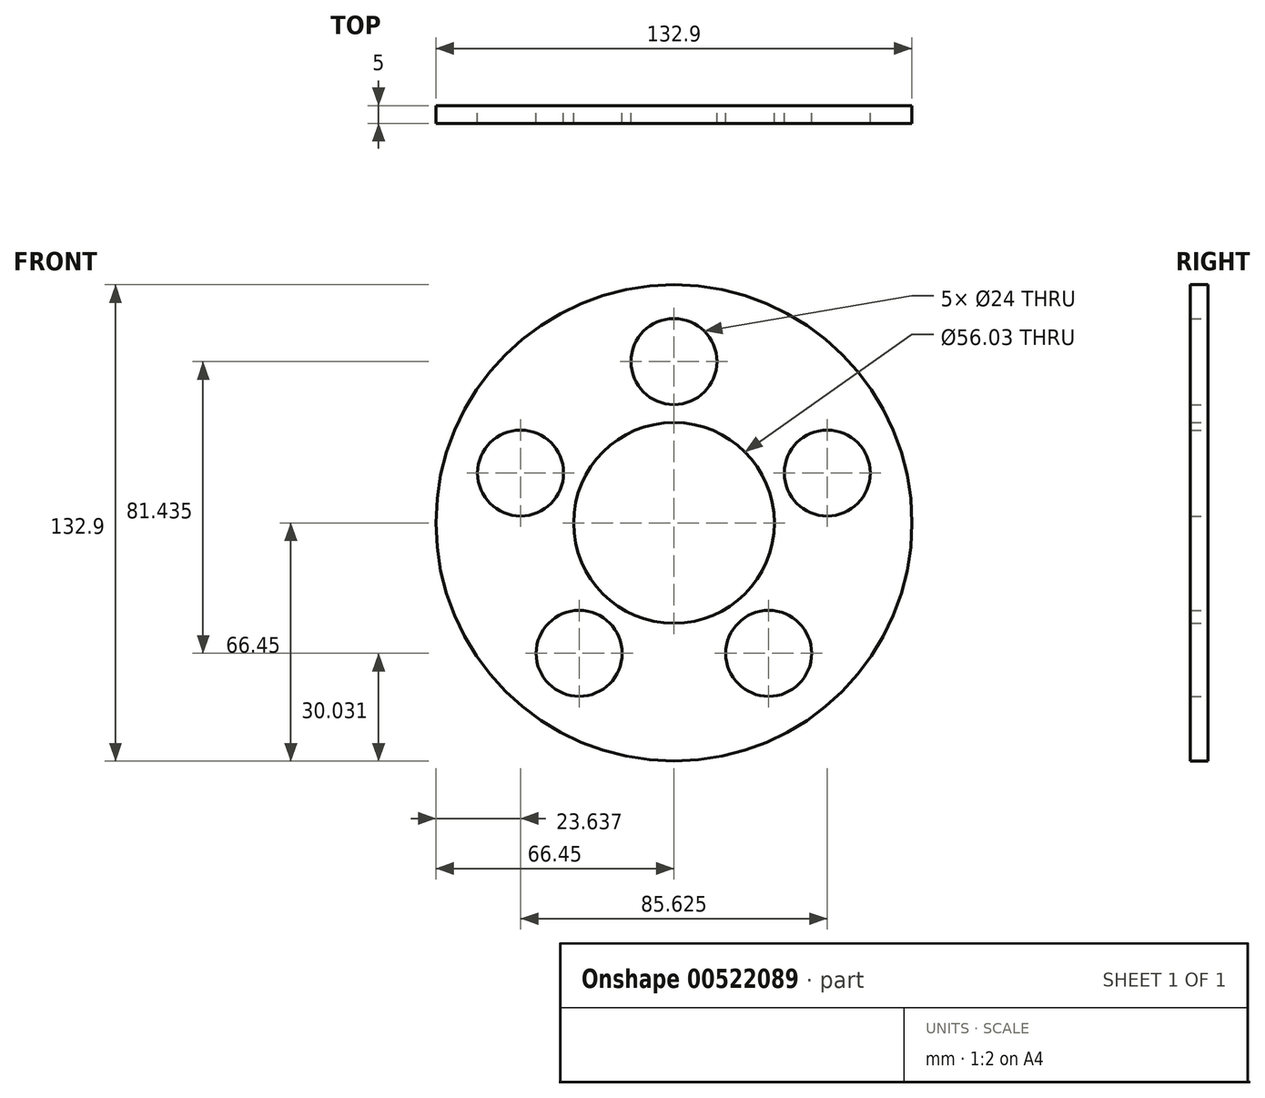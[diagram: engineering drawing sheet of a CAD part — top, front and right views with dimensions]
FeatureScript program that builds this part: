
annotation { "Feature Type Name" : "Feature", "Feature Type Description" : "" }
export const myFeature = defineFeature(function(context is Context, id is Id, definition is map)
    precondition{}
    {
        {
            var Q0;
            Q0=qCreatedBy(makeId("Front.planeOp"),FACE);
            var sketch = newSketch(context, id + "F0", { "sketchPlane" : qUnion([Q0])});
            skCircle(sketch, "E0", {"center": v(0, 0) * mm, "radius": 66.45 * mm});
            skCircle(sketch, "E1", {"center": v(0, 0) * mm, "radius": 28.02 * mm});
            skCircle(sketch, "E2", {"center": v(0, 45.02) * mm, "radius": 12 * mm});
            skCircle(sketch, "E3.1.0", {"center": v(-42.81, 13.91) * mm, "radius": 12 * mm});
            skCircle(sketch, "E3.2.0", {"center": v(-26.46, -36.42) * mm, "radius": 12 * mm});
            skCircle(sketch, "E3.3.0", {"center": v(26.46, -36.42) * mm, "radius": 12 * mm});
            skCircle(sketch, "E3.4.0", {"center": v(42.81, 13.91) * mm, "radius": 12 * mm});
            skSolve(sketch);
        }
        {
            var Q0;
            Q0 = qSketchRegion(id + "F0", true);
            extrude(context, id + "F1", {"entities" : qUnion([Q0]), "depth" : 5 * mm, "offsetDistance" : 25 * mm});
        }
    });
